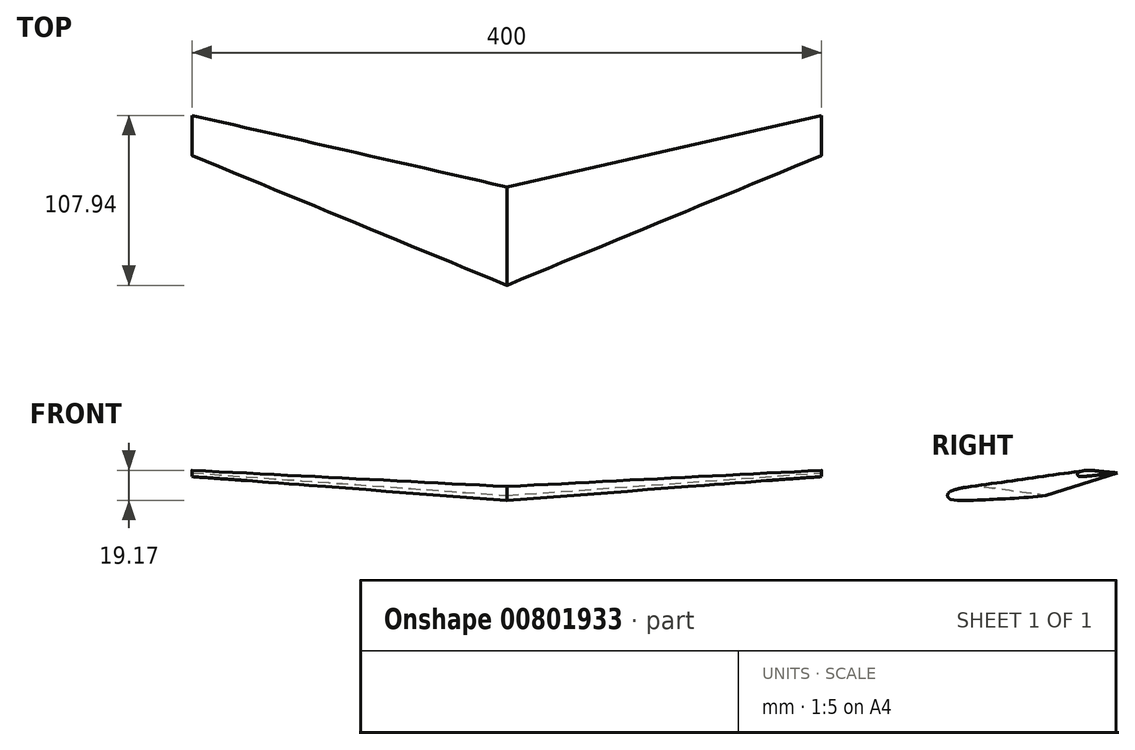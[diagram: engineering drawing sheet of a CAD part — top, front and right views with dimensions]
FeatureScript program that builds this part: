
annotation { "Feature Type Name" : "Feature", "Feature Type Description" : "" }
export const myFeature = defineFeature(function(context is Context, id is Id, definition is map)
    precondition{}
    {
        {
            var Q0;
            Q0=qCreatedBy(makeId("Right.planeOp"),FACE);
            cPlane(context, id + "F0", {"entities" : qUnion([Q0]), "cplaneType" : CPlaneType.OFFSET, "offset" : 200 * mm, "width" : 150 * mm, "height" : 150 * mm});
        }
        {
            var Q0;
            Q0=qCreatedBy(makeId("Right.planeOp"),FACE);
            var sketch = newSketch(context, id + "F1", { "sketchPlane" : qUnion([Q0])});
            skLineSegment(sketch, "E0", {"start": v(0, 0) * mm, "end": v(-60, 0) * mm, "construction": true});
            skArc(sketch, "E1", {"start": v(-61.27, 2.15) * mm, "mid": v(-62.47, -0.39) * mm, "end": v(-60.55, -2.44) * mm});
            skFitSpline(sketch, "E2", {"points": [v(-61.27, 2.15) * mm, v(-49, 5.42) * mm, v(-38.04, 5.3) * mm, v(-22.7, 3.27) * mm, v(0, 0) * mm], "startDerivative": vector(39.9, 23.47) * mm, "endDerivative": vector(57.57, -12.1) * mm});
            skFitSpline(sketch, "E3", {"points": [v(-60.55, -2.44) * mm, v(-43.14, -3) * mm, v(-23.92, -1.97) * mm, v(0, 0) * mm], "startDerivative": vector(43.91, -9.81) * mm, "endDerivative": vector(57.9, 9.37) * mm});
            skSolve(sketch);
        }
        {
            var Q0;
            Q0=qCreatedBy(id+"F0.planeOp",FACE);
            var sketch = newSketch(context, id + "F2", { "sketchPlane" : qUnion([Q0])});
            skLineSegment(sketch, "E4", {"start": v(45.44, 14.36) * mm, "end": v(21.52, 13.46) * mm, "construction": true});
            skCircle(sketch, "E5", {"center": v(21.52, 13.46) * mm, "radius": 1.5 * mm});
            skFitSpline(sketch, "E6", {"points": [v(45.44, 14.36) * mm, v(29.35, 15.92) * mm, v(26.2, 15.95) * mm, v(21.03, 14.88) * mm], "startDerivative": vector(-82.87, 6.32) * mm, "endDerivative": vector(-29.5, -10.35) * mm});
            skFitSpline(sketch, "E7", {"points": [v(45.44, 14.36) * mm, v(26.54, 12.28) * mm, v(21.61, 11.97) * mm], "startDerivative": vector(-45.34, -5.74) * mm, "endDerivative": vector(-26.58, -1.59) * mm});
            skSolve(sketch);
        }
        {
            var Q0;
            Q0 = qSketchRegion(id + "F1", true);
            var Q1;
            Q1 = qSketchRegion(id + "F2", true);
            loft(context, id + "F3", {"sheetProfilesArray" : [{ "sheetProfileEntities" : qUnion([Q0]) }, { "sheetProfileEntities" : qUnion([Q1]) }]});
        }
        {
            var Q0;
            Q0=makeQuery(id+"F3.opLoft","SWEPT_BODY",BODY,{"disambiguationData":[OSD([makeQuery(id+"F1.imprint","IMPRINT",FACE,{"disambiguationData":[TD([[makeQuery(id+"F1.imprint","IMPRINT",EDGE,{"derivedFrom":sQuery(id+"F1.wireOp",EDGE,"E1")}),1.0]])]}),makeQuery(id+"F2.imprint","IMPRINT",FACE,{"disambiguationData":[TD([[makeQuery(id+"F2.imprint","IMPRINT",EDGE,{"derivedFrom":sQuery(id+"F2.wireOp",EDGE,"Ep2JhIVR-b4vx-L6jj-cGfd-9NGOg68FnzgV")}),1.0]])]})])]});
            var Q1;
            Q1=qCreatedBy(makeId("Right.planeOp"),FACE);
            mirror(context, id + "F4", {"operationType" : NewBodyOperationType.ADD, "entities" : qUnion([Q0]), "mirrorPlane" : qUnion([Q1])});
        }
    });
